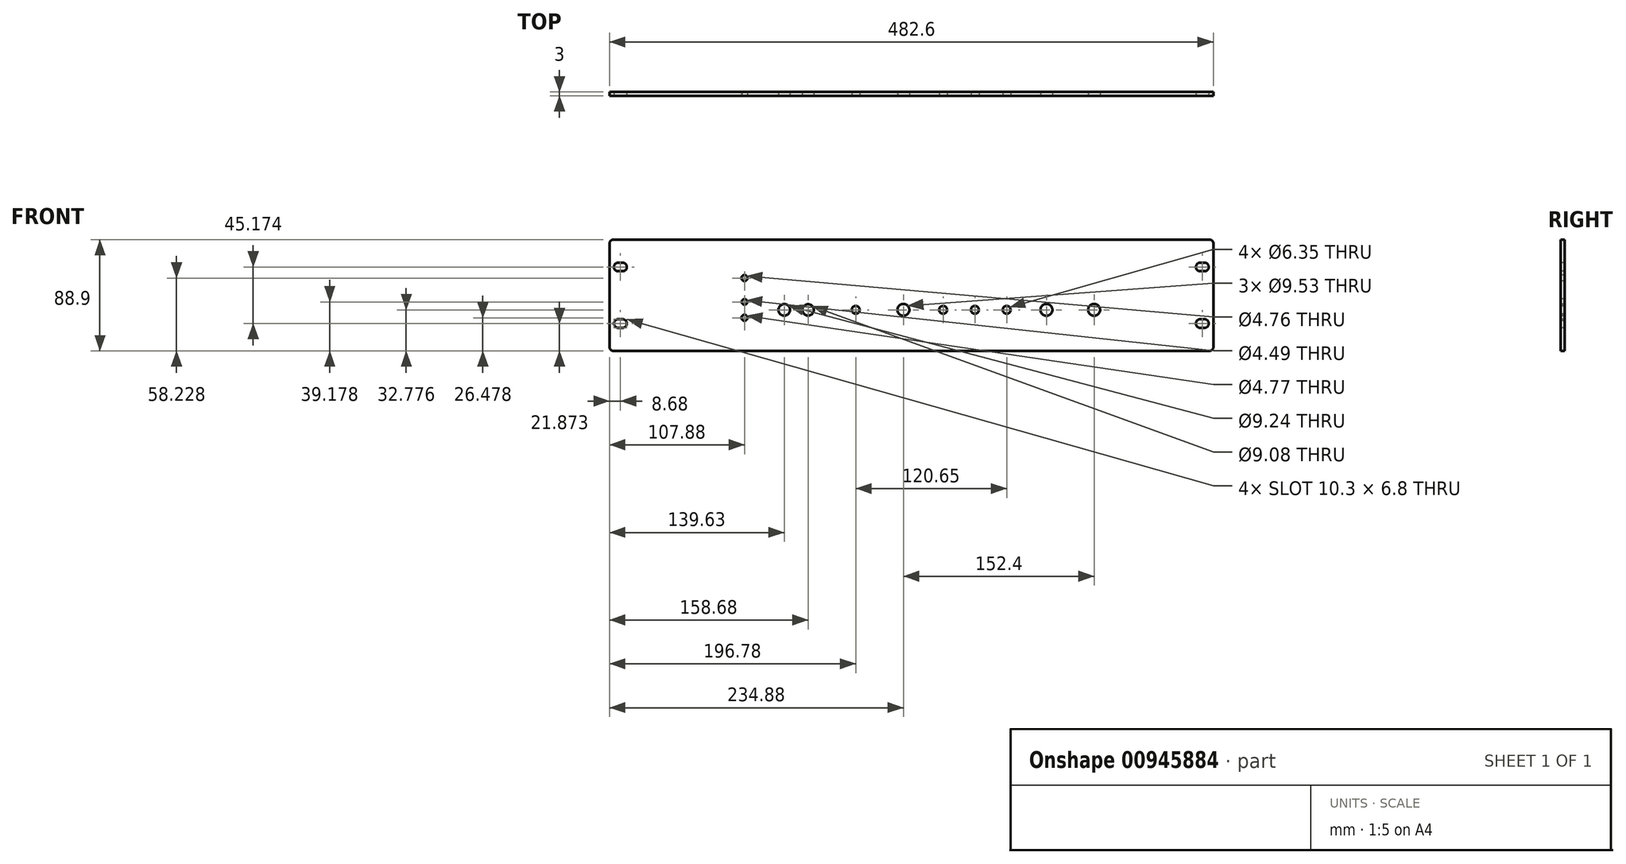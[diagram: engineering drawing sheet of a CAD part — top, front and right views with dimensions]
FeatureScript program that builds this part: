
annotation { "Feature Type Name" : "Feature", "Feature Type Description" : "" }
export const myFeature = defineFeature(function(context is Context, id is Id, definition is map)
    precondition{}
    {
        {
            var Q0;
            Q0=qCreatedBy(makeId("Front.planeOp"),FACE);
            var sketch = newSketch(context, id + "F0", { "sketchPlane" : qUnion([Q0])});
            skLineSegment(sketch, "E0.bottom", {"start": v(241.37, -44.46) * mm, "end": v(-241.23, -44.46) * mm});
            skLineSegment(sketch, "E0.top", {"start": v(241.37, 44.44) * mm, "end": v(-241.23, 44.44) * mm});
            skLineSegment(sketch, "E0.left", {"start": v(241.37, -44.46) * mm, "end": v(241.37, 44.44) * mm});
            skLineSegment(sketch, "E0.right", {"start": v(-241.23, -44.46) * mm, "end": v(-241.23, 44.44) * mm});
            skSolve(sketch);
        }
        {
            var Q0;
            Q0=makeQuery(id+"F0.imprint","IMPRINT",FACE,{"disambiguationData":[TD([[makeQuery(id+"F0.imprint","IMPRINT",EDGE,{"derivedFrom":sQuery(id+"F0.wireOp",EDGE,"E0.bottom")}),-1.0]])]});
            extrude(context, id + "F1", {"entities" : qUnion([Q0]), "oppositeDirection" : true, "depth" : 3 * mm, "offsetDistance" : 25 * mm});
        }
        {
            var Q0;
            Q0=makeQuery(id+"F1.opExtrude","SWEPT_EDGE",EDGE,{"disambiguationData":[OSD([sQuery(id+"F0.wireOp",EDGE,"E0.top"),sQuery(id+"F0.wireOp",EDGE,"E0.right")])]});
            var Q1;
            Q1=makeQuery(id+"F1.opExtrude","SWEPT_EDGE",EDGE,{"disambiguationData":[OSD([sQuery(id+"F0.wireOp",EDGE,"E0.top"),sQuery(id+"F0.wireOp",EDGE,"E0.left")])]});
            var Q2;
            Q2=makeQuery(id+"F1.opExtrude","SWEPT_EDGE",EDGE,{"disambiguationData":[OSD([sQuery(id+"F0.wireOp",EDGE,"E0.bottom"),sQuery(id+"F0.wireOp",EDGE,"E0.left")])]});
            var Q3;
            Q3=makeQuery(id+"F1.opExtrude","SWEPT_EDGE",EDGE,{"disambiguationData":[OSD([sQuery(id+"F0.wireOp",EDGE,"E0.bottom"),sQuery(id+"F0.wireOp",EDGE,"E0.right")])]});
            fillet(context, id + "F2", {"entities" : qUnion([Q0, Q1, Q2, Q3]), "radius" : 3 * mm, "tangentPropagation" : true, "allowEdgeOverflow" : false});
        }
        {
            var Q0;
            Q0=qCreatedBy(makeId("Front.planeOp"),FACE);
            var sketch = newSketch(context, id + "F3", { "sketchPlane" : qUnion([Q0])});
            skArc(sketch, "E1", {"start": v(-230.8, 19.19) * mm, "mid": v(-227.4, 22.59) * mm, "end": v(-230.8, 25.99) * mm});
            skArc(sketch, "E2", {"start": v(-234.3, 25.99) * mm, "mid": v(-237.7, 22.59) * mm, "end": v(-234.3, 19.19) * mm});
            skLineSegment(sketch, "E3", {"start": v(-234.3, 25.99) * mm, "end": v(-230.8, 25.99) * mm});
            skLineSegment(sketch, "E4", {"start": v(-234.3, 19.19) * mm, "end": v(-230.8, 19.19) * mm});
            skArc(sketch, "E5.MirrorCS", {"start": v(230.8, 19.19) * mm, "mid": v(227.4, 22.59) * mm, "end": v(230.8, 25.99) * mm});
            skLineSegment(sketch, "E6.MirrorCS", {"start": v(234.3, 25.99) * mm, "end": v(230.8, 25.99) * mm});
            skArc(sketch, "E7.MirrorCS", {"start": v(234.3, 25.99) * mm, "mid": v(237.7, 22.59) * mm, "end": v(234.3, 19.19) * mm});
            skLineSegment(sketch, "E8.MirrorCS", {"start": v(234.3, 19.19) * mm, "end": v(230.8, 19.19) * mm});
            skArc(sketch, "E9.MirrorCS", {"start": v(234.3, -25.99) * mm, "mid": v(237.7, -22.59) * mm, "end": v(234.3, -19.19) * mm});
            skArc(sketch, "E10.MirrorCS", {"start": v(230.8, -19.19) * mm, "mid": v(227.4, -22.59) * mm, "end": v(230.8, -25.99) * mm});
            skLineSegment(sketch, "E11.MirrorCS", {"start": v(234.3, -19.19) * mm, "end": v(230.8, -19.19) * mm});
            skLineSegment(sketch, "E12.MirrorCS", {"start": v(234.3, -25.99) * mm, "end": v(230.8, -25.99) * mm});
            skArc(sketch, "E13.MirrorCS", {"start": v(-230.8, -19.19) * mm, "mid": v(-227.4, -22.59) * mm, "end": v(-230.8, -25.99) * mm});
            skLineSegment(sketch, "E14.MirrorCS", {"start": v(-234.3, -25.99) * mm, "end": v(-230.8, -25.99) * mm});
            skArc(sketch, "E15.MirrorCS", {"start": v(-234.3, -25.99) * mm, "mid": v(-237.7, -22.59) * mm, "end": v(-234.3, -19.19) * mm});
            skLineSegment(sketch, "E16.MirrorCS", {"start": v(-234.3, -19.19) * mm, "end": v(-230.8, -19.19) * mm});
            skCircle(sketch, "E17", {"center": v(-133.35, 13.77) * mm, "radius": 2.38 * mm});
            skLineSegment(sketch, "E18", {"start": v(-247.85, 0) * mm, "end": v(247.54, 0) * mm, "construction": true});
            skLineSegment(sketch, "E19", {"start": v(-133.35, 13.77) * mm, "end": v(-133.35, -37.14) * mm, "construction": true});
            skLineSegment(sketch, "E20", {"start": v(-133.35, -11.68) * mm, "end": v(161.84, -11.68) * mm, "construction": true});
            skCircle(sketch, "E21", {"center": v(-133.35, -5.28) * mm, "radius": 2.25 * mm});
            skCircle(sketch, "E22", {"center": v(-133.35, -17.98) * mm, "radius": 2.38 * mm});
            skCircle(sketch, "E23", {"center": v(-101.6, -11.68) * mm, "radius": 4.62 * mm});
            skCircle(sketch, "E24", {"center": v(-82.55, -11.68) * mm, "radius": 4.54 * mm});
            skCircle(sketch, "E25", {"center": v(-44.45, -11.68) * mm, "radius": 3.18 * mm});
            skCircle(sketch, "E26", {"center": v(-6.35, -11.68) * mm, "radius": 4.76 * mm});
            skCircle(sketch, "E27", {"center": v(25.4, -11.68) * mm, "radius": 3.18 * mm});
            skCircle(sketch, "E28", {"center": v(50.8, -11.68) * mm, "radius": 3.18 * mm});
            skCircle(sketch, "E29", {"center": v(76.2, -11.68) * mm, "radius": 3.18 * mm});
            skCircle(sketch, "E30", {"center": v(107.95, -11.68) * mm, "radius": 4.76 * mm});
            skCircle(sketch, "E31", {"center": v(146.05, -11.68) * mm, "radius": 4.76 * mm});
            skLineSegment(sketch, "E32", {"start": v(0, 0) * mm, "end": v(0, -11.68) * mm, "construction": true});
            skSolve(sketch);
        }
        {
            var Q0;
            Q0=qSketchRegion(id+"F3",true);
            extrude(context, id + "F4", {"entities" : qUnion([Q0]), "operationType" : NewBodyOperationType.REMOVE, "endBound" : BoundingType.UP_TO_NEXT, "oppositeDirection" : true, "depth" : 25 * mm, "offsetDistance" : 25 * mm});
        }
    });
